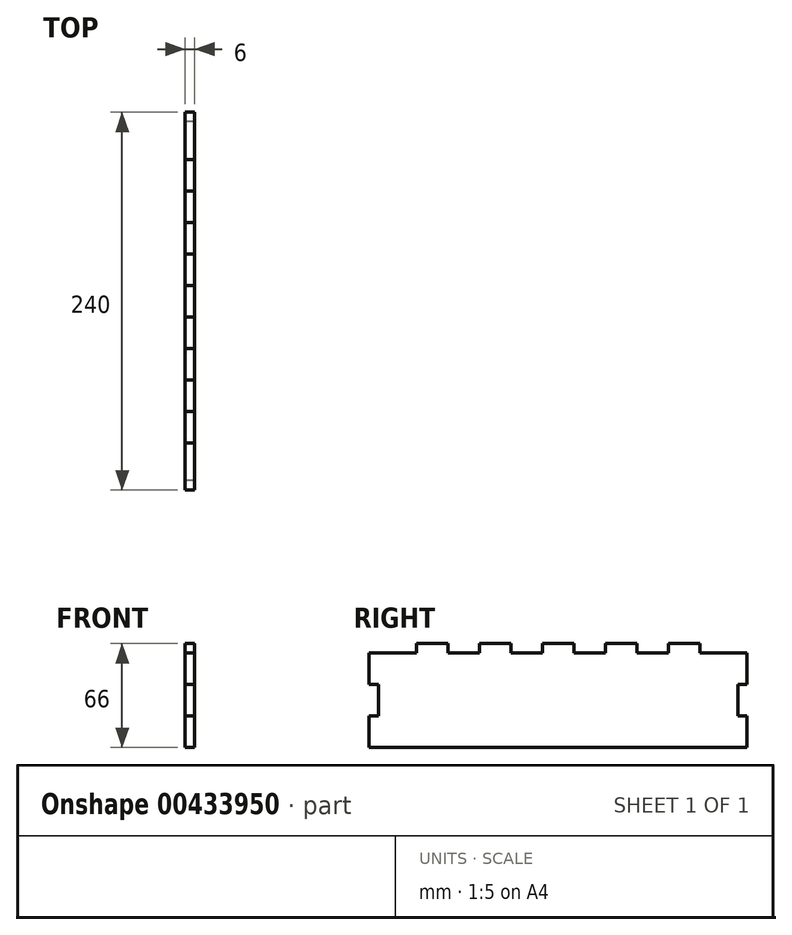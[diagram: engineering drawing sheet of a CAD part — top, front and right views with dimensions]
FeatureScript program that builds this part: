
annotation { "Feature Type Name" : "Feature", "Feature Type Description" : "" }
export const myFeature = defineFeature(function(context is Context, id is Id, definition is map)
    precondition{}
    {
        {
            var Q0;
            Q0=qCreatedBy(makeId("Top.planeOp"),FACE);
            var sketch = newSketch(context, id + "F0", { "sketchPlane" : qUnion([Q0])});
            skLineSegment(sketch, "E0.bottom", {"start": v(3, -120) * mm, "end": v(-3, -120) * mm});
            skLineSegment(sketch, "E0.top", {"start": v(3, 120) * mm, "end": v(-3, 120) * mm});
            skLineSegment(sketch, "E0.left", {"start": v(3, -120) * mm, "end": v(3, 120) * mm});
            skLineSegment(sketch, "E0.right", {"start": v(-3, -120) * mm, "end": v(-3, 120) * mm});
            skPoint(sketch, "E0.middle", {"position": v(0, 0) * mm});
            skSolve(sketch);
        }
        {
            var Q0;
            Q0=makeQuery(id+"F0.imprint","IMPRINT",FACE,{"disambiguationData":[TD([[makeQuery(id+"F0.imprint","IMPRINT",EDGE,{"derivedFrom":sQuery(id+"F0.wireOp",EDGE,"E0.bottom")}),-1.0]])]});
            extrude(context, id + "F1", {"entities" : qUnion([Q0]), "depth" : 60 * mm});
        }
        {
            var Q0;
            Q0=makeQuery(id+"F1.opExtrude","SWEPT_FACE",FACE,{"disambiguationData":[OSD([sQuery(id+"F0.wireOp",EDGE,"E0.right")])]});
            var sketch = newSketch(context, id + "F2", { "sketchPlane" : qUnion([Q0])});
            skLineSegment(sketch, "E1", {"start": v(-120, 40) * mm, "end": v(-114, 40) * mm});
            skLineSegment(sketch, "E2", {"start": v(-114, 40) * mm, "end": v(-114, 20) * mm});
            skLineSegment(sketch, "E3", {"start": v(-114, 20) * mm, "end": v(-120, 20) * mm});
            skLineSegment(sketch, "E4.MirrorCS", {"start": v(114, 40) * mm, "end": v(114, 20) * mm});
            skLineSegment(sketch, "E5.MirrorCS", {"start": v(114, 20) * mm, "end": v(120, 20) * mm});
            skLineSegment(sketch, "E6.MirrorCS", {"start": v(120, 40) * mm, "end": v(114, 40) * mm});
            skLineSegment(sketch, "E7", {"start": v(90, 60) * mm, "end": v(90, 66) * mm});
            skLineSegment(sketch, "E8", {"start": v(90, 66) * mm, "end": v(70, 66) * mm});
            skLineSegment(sketch, "E9", {"start": v(70, 66) * mm, "end": v(70, 60) * mm});
            skLineSegment(sketch, "E10.1.0.0", {"start": v(50, 60) * mm, "end": v(50, 66) * mm});
            skLineSegment(sketch, "E10.1.0.1", {"start": v(30, 66) * mm, "end": v(30, 60) * mm});
            skLineSegment(sketch, "E10.1.0.2", {"start": v(50, 66) * mm, "end": v(30, 66) * mm});
            skLineSegment(sketch, "E10.2.0.0", {"start": v(10, 60) * mm, "end": v(10, 66) * mm});
            skLineSegment(sketch, "E10.2.0.1", {"start": v(-10, 66) * mm, "end": v(-10, 60) * mm});
            skLineSegment(sketch, "E10.2.0.2", {"start": v(10, 66) * mm, "end": v(-10, 66) * mm});
            skLineSegment(sketch, "E10.3.0.0", {"start": v(-30, 60) * mm, "end": v(-30, 66) * mm});
            skLineSegment(sketch, "E10.3.0.1", {"start": v(-50, 66) * mm, "end": v(-50, 60) * mm});
            skLineSegment(sketch, "E10.3.0.2", {"start": v(-30, 66) * mm, "end": v(-50, 66) * mm});
            skLineSegment(sketch, "E10.4.0.0", {"start": v(-70, 60) * mm, "end": v(-70, 66) * mm});
            skLineSegment(sketch, "E10.4.0.1", {"start": v(-90, 66) * mm, "end": v(-90, 60) * mm});
            skLineSegment(sketch, "E10.4.0.2", {"start": v(-70, 66) * mm, "end": v(-90, 66) * mm});
            skLineSegment(sketch, "E10.direction1", {"start": v(70, 60) * mm, "end": v(30, 60) * mm, "construction": true});
            skSolve(sketch);
        }
        {
            var Q0;
            {var subQ0=sQuery(id+"F2.wireOp",EDGE,"E1");Q0=makeQuery(id+"F2.imprint","IMPRINT",FACE,{"disambiguationData":[TD([[makeQuery(id+"F2.imprint","IMPRINT",EDGE,{"derivedFrom":subQ0}),-1.0]])]});}
            var Q1;
            Q1=makeQuery(id+"F2.imprint","IMPRINT",FACE,{"disambiguationData":[TD([[makeQuery(id+"F2.imprint","IMPRINT",EDGE,{"derivedFrom":sQuery(id+"F2.wireOp",EDGE,"E4.MirrorCS")}),1.0]])]});
            extrude(context, id + "F3", {"entities" : qUnion([Q0, Q1]), "operationType" : NewBodyOperationType.REMOVE, "endBound" : BoundingType.THROUGH_ALL, "oppositeDirection" : true, "depth" : 25 * mm});
        }
        {
            var Q0;
            {var subQ0=sQuery(id+"F2.wireOp",EDGE,"E7");Q0=makeQuery(id+"F2.imprint","IMPRINT",FACE,{"disambiguationData":[TD([[makeQuery(id+"F2.imprint","IMPRINT",EDGE,{"derivedFrom":subQ0}),1.0]])]});}
            var Q1;
            {var subQ0=sQuery(id+"F2.wireOp",EDGE,"E10.1.0.0");Q1=makeQuery(id+"F2.imprint","IMPRINT",FACE,{"disambiguationData":[TD([[makeQuery(id+"F2.imprint","IMPRINT",EDGE,{"derivedFrom":subQ0}),1.0]])]});}
            var Q2;
            {var subQ0=sQuery(id+"F2.wireOp",EDGE,"E10.2.0.0");Q2=makeQuery(id+"F2.imprint","IMPRINT",FACE,{"disambiguationData":[TD([[makeQuery(id+"F2.imprint","IMPRINT",EDGE,{"derivedFrom":subQ0}),1.0]])]});}
            var Q3;
            {var subQ0=sQuery(id+"F2.wireOp",EDGE,"E10.3.0.0");Q3=makeQuery(id+"F2.imprint","IMPRINT",FACE,{"disambiguationData":[TD([[makeQuery(id+"F2.imprint","IMPRINT",EDGE,{"derivedFrom":subQ0}),1.0]])]});}
            var Q4;
            {var subQ0=sQuery(id+"F2.wireOp",EDGE,"E10.4.0.0");Q4=makeQuery(id+"F2.imprint","IMPRINT",FACE,{"disambiguationData":[TD([[makeQuery(id+"F2.imprint","IMPRINT",EDGE,{"derivedFrom":subQ0}),1.0]])]});}
            extrude(context, id + "F4", {"entities" : qUnion([Q0, Q1, Q2, Q3, Q4]), "operationType" : NewBodyOperationType.ADD, "oppositeDirection" : true, "depth" : 6 * mm});
        }
    });
